# Revit family: Storage-Teknion-MXCES-Elevated_Credenza_with_Specialty_Top-Expansion_Meeting-R2023
name_source: partatom
category: Furniture
units: mm (PartAtom-declared; Revit-internal decimal feet)

## family parameters
Always vertical = Yes
Cut with Voids When Loaded = No
Enable Cutting in Views = No
OmniClass Number = 23.40.20.00
OmniClass Title = General Furniture and Specialties
Render Appearance Source = Family Geometry
Room Calculation Point = No
Shared = Yes
Work Plane-Based = No

## types (6) — shared parameters
Assembly Code = E2020200
Manufacturer = Teknion
Manufacturer Fax = 416.661.4586
Part Number = MXCES
Product Documentation Link = http://www.teknion.com
Product Line = Credenzas
Product Page URL = http://www.teknion.com
Series = Meeting Expansion
Sustainability Data = https://www.teknion.com
URL = www.teknion.com
Unit Weight URL = http://www.teknion.com
Warranty = http://www.teknion.com
zero-valued in all types: Default Elevation

## per-type parameters (varying)
| type | 1 Pull-Out Bin | 2 Pull-Out Bins | Bin 1 | Bin 2 | Blade Foot | Description | Model | No Pull-Out Bin | Square Foot |
| No Pull-Out Bin / Square Foot | No | No | No | No | No | Meeting Expansion, Elevated Credenzas with Specialty Top - No Pull-Out Bin, Square Foot | MXCESS______N | Yes | Yes |
| 1 Pull-Out Bin / Square Foot | Yes | No | Yes | No | No | Meeting Expansion, Elevated Credenzas with Specialty Top - 1 Pull-Out Bin, Square Foot | MXCESS______R / MXCESS______L | No | Yes |
| 2 Pull-Out Bins / Square Foot | No | Yes | Yes | Yes | No | Meeting Expansion, Elevated Credenzas with Specialty Top - 2 Pull-Out Bins, Square Foot | MXCESS______T / MXCESS______V | No | Yes |
| 1 Pull-Out Bin / Blade Foot | Yes | No | Yes | No | Yes | Meeting Expansion, Elevated Credenzas with Specialty Top - 1 Pull-Out Bin, Blade Foot | MXCESB______R / MXCESB______L | No | No |
| 2 Pull-Out Bins / Blade Foot | No | Yes | Yes | Yes | Yes | Meeting Expansion, Elevated Credenzas with Specialty Top - 2 Pull-Out Bins, Blade Foot | MXCESB______T / MXCESB______V | No | No |
| No Pull-Out Bin / Blade Foot | No | No | No | No | Yes | Meeting Expansion, Elevated Credenzas with Specialty Top - No Pull-Out Bin, Blade Foot | MXCESB______N | Yes | No |

## geometry (parser evidence)
native form markers: Sweep x3
no freeform markers — native parametric forms only
